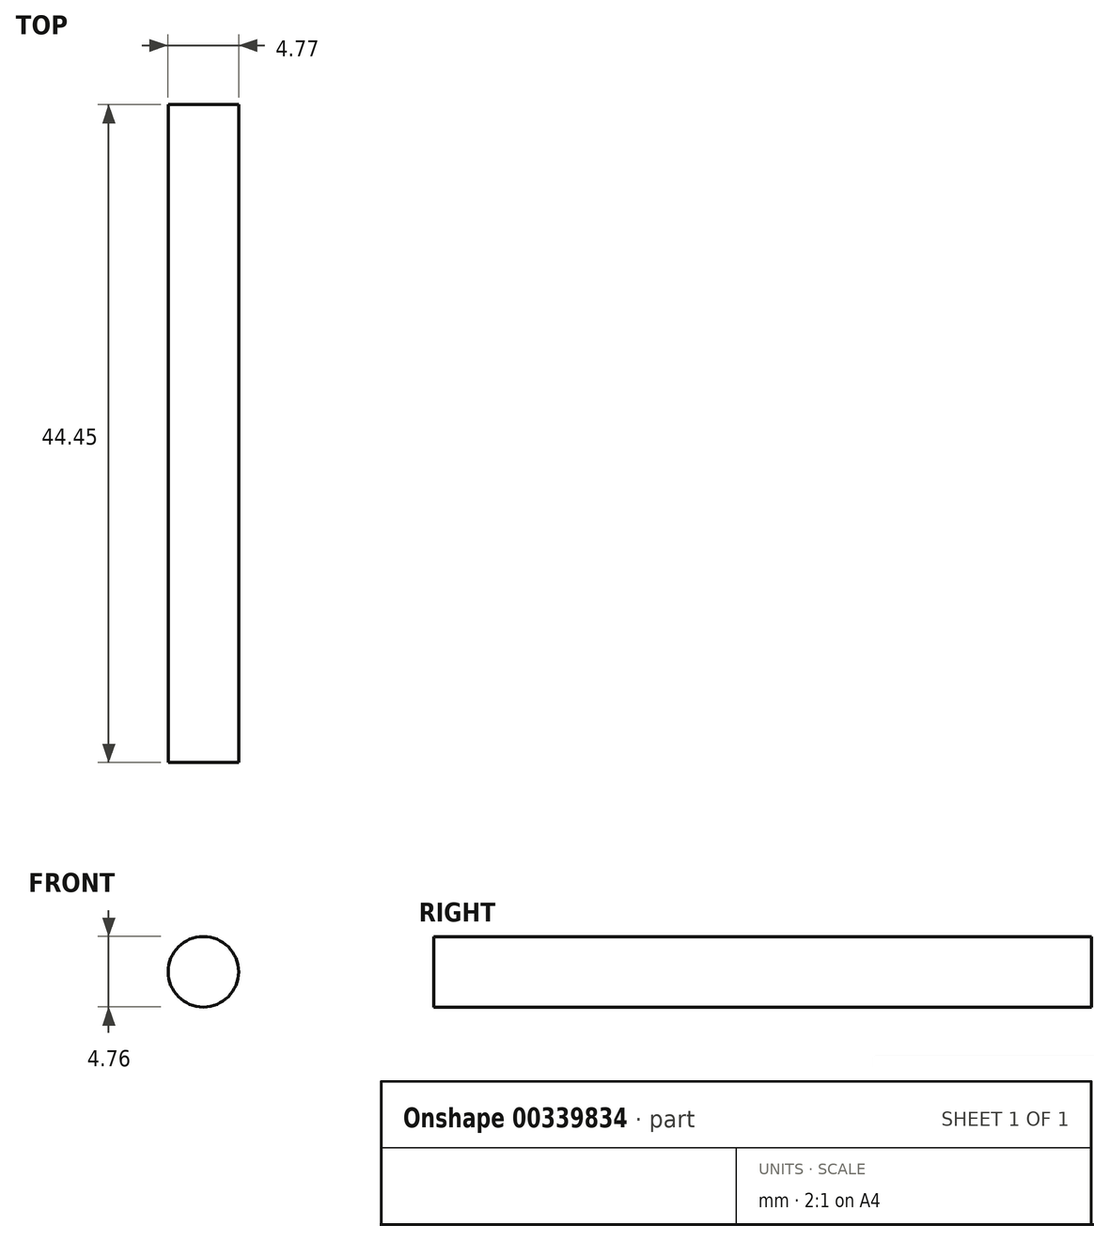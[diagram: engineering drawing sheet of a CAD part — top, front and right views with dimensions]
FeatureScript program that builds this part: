
annotation { "Feature Type Name" : "Feature", "Feature Type Description" : "" }
export const myFeature = defineFeature(function(context is Context, id is Id, definition is map)
    precondition{}
    {
        {
            var Q0;
            Q0=qCreatedBy(makeId("Front.planeOp"),FACE);
            var sketch = newSketch(context, id + "F0", { "sketchPlane" : qUnion([Q0])});
            skCircle(sketch, "E0", {"center": v(-37.34, 23.25) * mm, "radius": 2.38 * mm});
            skSolve(sketch);
        }
        {
            var Q0;
            Q0=makeQuery(id+"F0.imprint","IMPRINT",FACE,{"disambiguationData":[TD([[makeQuery(id+"F0.imprint","IMPRINT",EDGE,{"derivedFrom":sQuery(id+"F0.wireOp",EDGE,"E0")}),1.0]])]});
            extrude(context, id + "F1", {"entities" : qUnion([Q0]), "oppositeDirection" : true, "depth" : 44.45 * mm});
        }
    });
